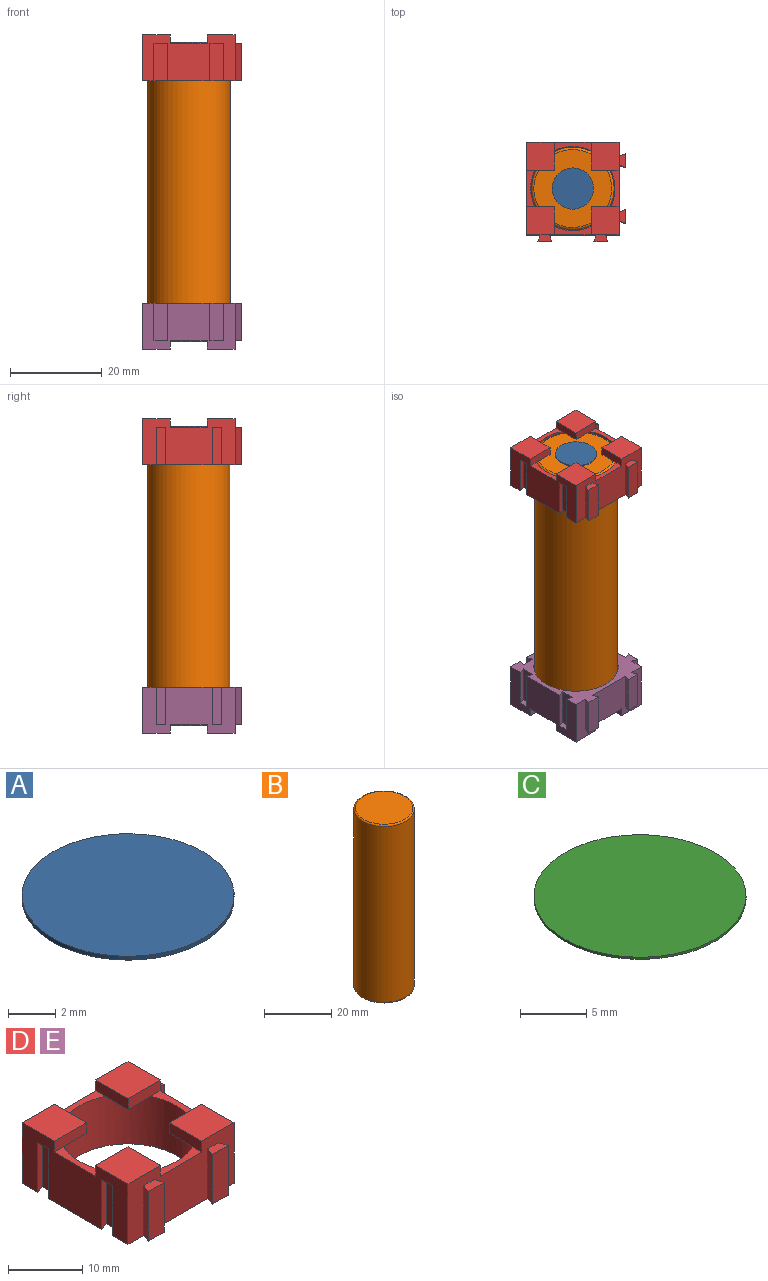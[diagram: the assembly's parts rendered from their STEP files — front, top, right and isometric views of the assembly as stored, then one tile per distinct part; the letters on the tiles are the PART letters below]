
ASSEMBLY  parts=5 mates=4
PART A: 3 faces, bbox 9x9x0.2 mm
  f0: cylinder r=4.5mm len=9mm, axis (0,0,-1), area 5.7mm2, adj f1,f2
  f1: plane 9x9mm, normal (0,0,1), area 63.6mm2, adj f0
  f2: plane 9x9mm, normal (0,0,-1), area 63.6mm2, adj f0
PART B: 7 faces, bbox 19.5x19.5x65 mm
  f0: cylinder r=9mm len=64mm, axis (0,0,-1), area 3619.1mm2, adj f5,f6
  f1: plane 17x17mm, normal (0,0,1), area 227mm2, adj f6
  f2: plane 17x17mm, normal (0,0,-1), area 25.9mm2, adj f3,f5
  f3: cylinder r=8mm len=16mm, axis (0,0,-1), area 10.1mm2, adj f2,f4
  f4: plane 16x16mm, normal (0,0,-1), area 201.1mm2, adj f3
  f5: torus R=8.5mm, axis (0,0,1), area 43.5mm2, adj f0,f2
  f6: torus R=8.5mm, axis (0,0,1), area 43.5mm2, adj f0,f1
PART C: 3 faces, bbox 16x16x0.2 mm
  f0: cylinder r=8mm len=16mm, axis (0,0,1), area 10.1mm2, adj f1,f2
  f1: plane 16x16mm, normal (0,0,-1), area 201.1mm2, adj f0
  f2: plane 16x16mm, normal (0,0,1), area 201.1mm2, adj f0
PART D: 58 faces, bbox 21.6x21.6x10 mm
  f0: plane 8x1.82mm, normal (0,0,1), area 9.6mm2, adj f26,f35,f39,f54
  f1: plane 3x1.4mm, normal (0,0,1), area 3.5mm2, adj f26,f27,f28,f29
  f2: plane 8x1.82mm, normal (0,0,1), area 9.6mm2, adj f19,f35,f49,f55
  f3: plane 3x1.4mm, normal (0,0,1), area 3.5mm2, adj f9,f10,f11,f33
  f4: plane 8x1.82mm, normal (0,0,1), area 9.6mm2, adj f18,f35,f43,f50
  f5: plane 8x1.82mm, normal (0,0,1), area 9.6mm2, adj f33,f35,f40,f44
  f6: plane 3x1.4mm, normal (0,0,1), area 3.5mm2, adj f8,f33,f34,f36
  f7: plane 3x1.4mm, normal (0,0,1), area 3.5mm2, adj f26,f30,f31,f32
  f8: plane 8.2x1.4mm, normal (-0.34,0.94,0), area 12.2mm2, adj f6,f33,f36,f37
  f9: plane 8.2x1.4mm, normal (-0.34,-0.94,0), area 12.2mm2, adj f3,f10,f33,f37
  f10: plane 8.2x3mm, normal (1,0,0), area 24.6mm2, adj f3,f9,f11,f37
  f11: plane 8.2x1.4mm, normal (-0.34,0.94,0), area 12.2mm2, adj f3,f10,f33,f37
  f12: plane 8.2x1.4mm, normal (-0.94,-0.34,0), area 12.2mm2, adj f13,f18,f37,f46
  f13: plane 8.2x3mm, normal (0,1,0), area 24.6mm2, adj f12,f14,f37,f46
  f14: plane 8.2x1.4mm, normal (0.94,-0.34,0), area 12.2mm2, adj f13,f18,f37,f46
  f15: plane 8.2x1.4mm, normal (-0.94,-0.34,0), area 12.2mm2, adj f16,f18,f37,f48
  f16: plane 8.2x3mm, normal (0,1,0), area 24.6mm2, adj f15,f17,f37,f48
  f17: plane 8.2x1.4mm, normal (0.94,-0.34,0), area 12.2mm2, adj f16,f18,f37,f48
  f18: plane 20.2x10mm, normal (0,1,0), area 154.8mm2, adj f4,f12,f14,f15,f17,f19,f33,f37
  f19: plane 20.2x10mm, normal (-1,0,0), area 154.8mm2, adj f2,f18,f20,f22,f23,f25,f26,f37
  f20: plane 8.2x1.4mm, normal (0.34,-0.94,0), area 12.2mm2, adj f19,f21,f37,f52
  f21: plane 8.2x3mm, normal (-1,0,0), area 24.6mm2, adj f20,f22,f37,f52
  f22: plane 8.2x1.4mm, normal (0.34,0.94,0), area 12.2mm2, adj f19,f21,f37,f52
  f23: plane 8.2x1.4mm, normal (0.34,-0.94,0), area 12.2mm2, adj f19,f24,f37,f57
  f24: plane 8.2x3mm, normal (-1,0,0), area 24.6mm2, adj f23,f25,f37,f57
  f25: plane 8.2x1.4mm, normal (0.34,0.94,0), area 12.2mm2, adj f19,f24,f37,f57
  f26: plane 20.2x10mm, normal (0,-1,0), area 154.8mm2, adj f0,f1,f7,f19,f27,f29,f30,f32
  f27: plane 8.2x1.4mm, normal (-0.94,0.34,0), area 12.2mm2, adj f1,f26,f28,f37
  f28: plane 8.2x3mm, normal (0,-1,0), area 24.6mm2, adj f1,f27,f29,f37
  f29: plane 8.2x1.4mm, normal (0.94,0.34,0), area 12.2mm2, adj f1,f26,f28,f37
  f30: plane 8.2x1.4mm, normal (-0.94,0.34,0), area 12.2mm2, adj f7,f26,f31,f37
  f31: plane 8.2x3mm, normal (0,-1,0), area 24.6mm2, adj f7,f30,f32,f37
  f32: plane 8.2x1.4mm, normal (0.94,0.34,0), area 12.2mm2, adj f7,f26,f31,f37
  f33: plane 20.2x10mm, normal (1,0,0), area 154.8mm2, adj f3,f5,f6,f8,f9,f11,f18,f26
  f34: plane 8.2x1.4mm, normal (-0.34,-0.94,0), area 12.2mm2, adj f6,f33,f36,f37
  f35: cylinder r=9.2mm len=18.4mm, axis (0,0,-1), area 474mm2, adj f0,f2,f4,f5,f37,f38,f42,f47
  f36: plane 8.2x3mm, normal (1,0,0), area 24.6mm2, adj f6,f8,f34,f37
  f37: plane 21.6x21.6mm, normal (0,0,-1), area 142.1mm2, adj f8,f9,f10,f11,f12,f13,f14,f15
  f38: plane 4.29x4.29mm, normal (0,0,-1), area 11.3mm2, adj f35,f39,f40
  f39: plane 6.1x1.8mm, normal (-1,0,0), area 11mm2, adj f0,f26,f38,f40,f41
  f40: plane 6.1x1.8mm, normal (0,1,0), area 11mm2, adj f5,f33,f38,f39,f41
  f41: plane 6.1x6.1mm, normal (0,0,1), area 37.2mm2, adj f26,f33,f39,f40
  f42: plane 4.29x4.29mm, normal (0,0,-1), area 11.3mm2, adj f35,f43,f44
  f43: plane 6.1x1.8mm, normal (-1,0,0), area 11mm2, adj f4,f18,f42,f44,f45
  f44: plane 6.1x1.8mm, normal (0,-1,0), area 11mm2, adj f5,f33,f42,f43,f45
  f45: plane 6.1x6.1mm, normal (0,0,1), area 37.2mm2, adj f18,f33,f43,f44
  f46: plane 3x1.4mm, normal (0,0,-1), area 3.5mm2, adj f12,f13,f14,f18
  f47: plane 4.29x4.29mm, normal (0,0,-1), area 11.3mm2, adj f35,f49,f50
  f48: plane 3x1.4mm, normal (0,0,-1), area 3.5mm2, adj f15,f16,f17,f18
  f49: plane 6.1x1.8mm, normal (0,-1,0), area 11mm2, adj f2,f19,f47,f50,f51
  f50: plane 6.1x1.8mm, normal (1,0,0), area 11mm2, adj f4,f18,f47,f49,f51
  f51: plane 6.1x6.1mm, normal (0,0,1), area 37.2mm2, adj f18,f19,f49,f50
  f52: plane 3x1.4mm, normal (0,0,-1), area 3.5mm2, adj f19,f20,f21,f22
  f53: plane 4.29x4.29mm, normal (0,0,-1), area 11.3mm2, adj f35,f54,f55
  f54: plane 6.1x1.8mm, normal (1,0,0), area 11mm2, adj f0,f26,f53,f55,f56
  f55: plane 6.1x1.8mm, normal (0,1,0), area 11mm2, adj f2,f19,f53,f54,f56
  f56: plane 6.1x6.1mm, normal (0,0,1), area 37.2mm2, adj f19,f26,f54,f55
  f57: plane 3x1.4mm, normal (0,0,-1), area 3.5mm2, adj f19,f23,f24,f25
PART E: same geometry as D
PLACE A t=(8.01,-18.13,3.64)mm
PLACE B t=(8.01,-18.13,3.64)mm
PLACE C t=(8.01,-18.13,3.44)mm
PLACE D t=(8.01,-18.13,60.44)mm
PLACE E rot(axis=(0.71,-0.71,0),180deg) t=(8.01,-18.13,11.84)mm
MATE fastened A.f0 <-> B.f0  axis (0,0,-1) through (8.01,-18.13,68.64)mm
MATE fastened D.f35 <-> B.f0  axis (0,0,-1) through (8.01,-18.13,68.64)mm
MATE fastened C.f0 <-> B.f3  axis (0,0,1) through (8.01,-18.13,3.64)mm
MATE fastened E.f35 <-> B.f0  axis (0,0,1) through (8.01,-18.13,3.64)mm
